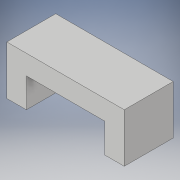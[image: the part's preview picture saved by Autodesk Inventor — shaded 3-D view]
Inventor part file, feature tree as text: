
AUTODESK INVENTOR PART (.ipt)
format: ipt  version: 2019 (Build 230136000, 136)  size: 106,496 bytes
history: native  units: in
note: dims shown in document units (in); Inventor stores cm internally (conversion verified against a paired STEP export)
features: extrude x2, sketch x2
ambient origin geometry x8: Origin, YZ Plane, XZ Plane, XY Plane, X Axis, Y Axis, Z Axis, Center Point
bodies: Solid1 (feature_tree)
feature tree (4):
  extrude  "Extrusion1"  Depth=0.3in TaperAngle=0.0deg
  extrude  "Extrusion2"  [1 undecoded]
  sketch  "Sketch1"  dims[d1=0.7874in d3=0.3937in d4=0.5in d5=0.2in d7=1.0in d11=1.0in d12=0.3in d13=0.0in]
  sketch  "Sketch3"  dims[d14=0.2in d15=0.0in]
note: 1 required parameter value undecoded (feature->parameter linkage not recoverable at this tier; creation-order binding heuristic only, values carry confidence <= 0.55)
